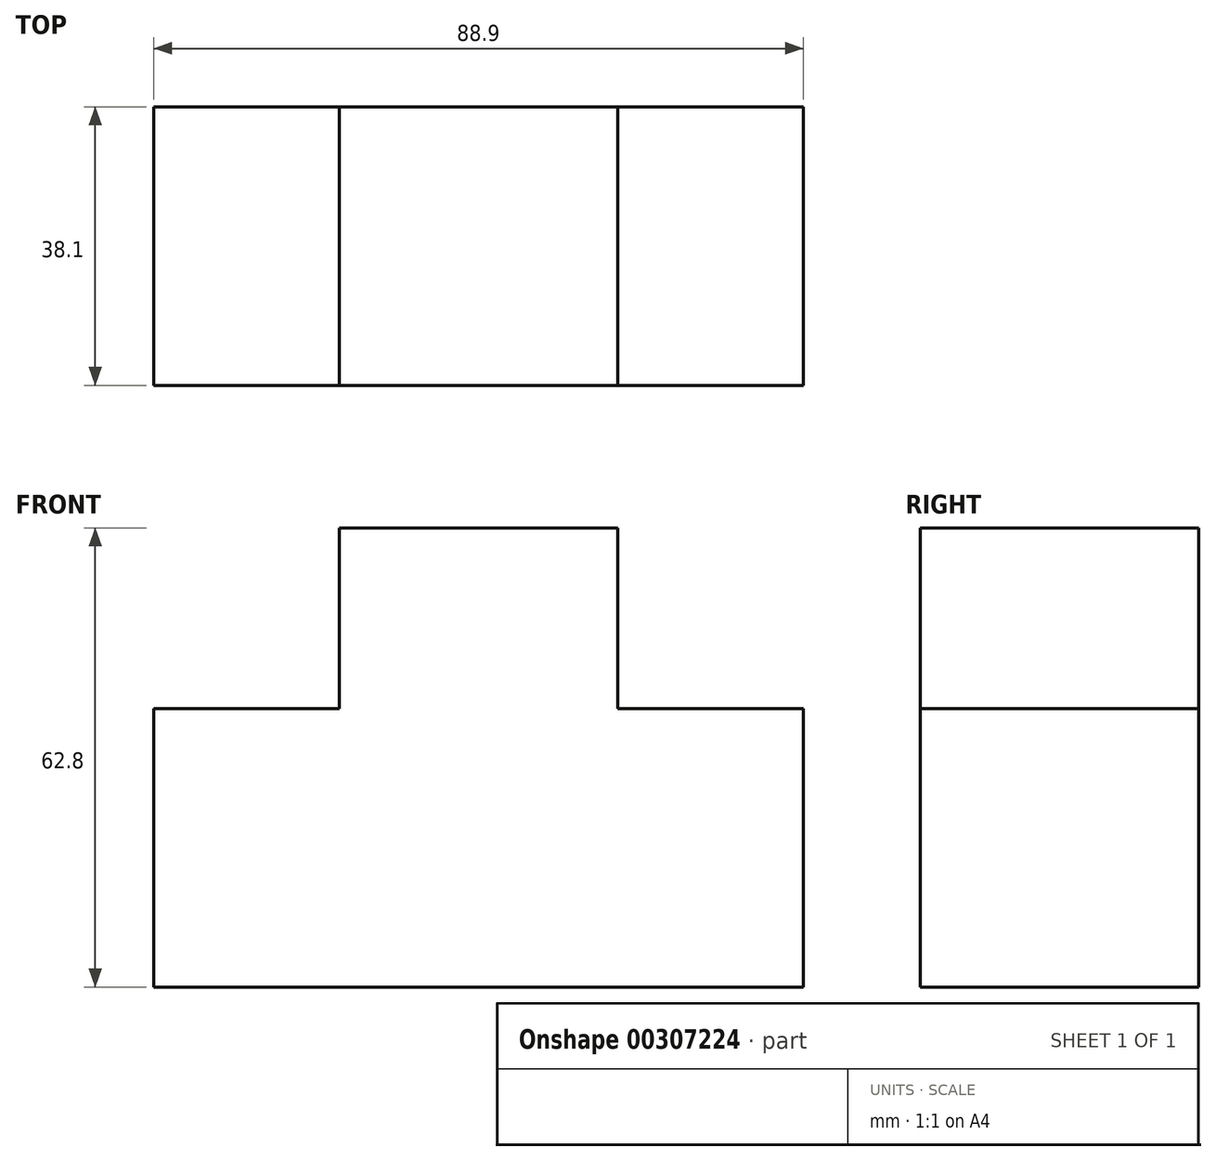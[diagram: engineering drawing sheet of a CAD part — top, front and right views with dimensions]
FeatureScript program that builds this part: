
annotation { "Feature Type Name" : "Feature", "Feature Type Description" : "" }
export const myFeature = defineFeature(function(context is Context, id is Id, definition is map)
    precondition{}
    {
        {
            var Q0;
            Q0=qCreatedBy(makeId("Front.planeOp"),FACE);
            var sketch = newSketch(context, id + "F0", { "sketchPlane" : qUnion([Q0])});
            skLineSegment(sketch, "E0", {"start": v(-42.03, -48.8) * mm, "end": v(46.87, -48.8) * mm});
            skLineSegment(sketch, "E1", {"start": v(46.87, -48.8) * mm, "end": v(46.87, -10.7) * mm});
            skLineSegment(sketch, "E2", {"start": v(46.87, -10.7) * mm, "end": v(21.47, -10.7) * mm});
            skLineSegment(sketch, "E3", {"start": v(21.47, -10.7) * mm, "end": v(21.47, 14) * mm});
            skLineSegment(sketch, "E4", {"start": v(21.47, 14) * mm, "end": v(-16.63, 14) * mm});
            skLineSegment(sketch, "E5", {"start": v(-16.63, 14) * mm, "end": v(-16.63, -10.7) * mm});
            skLineSegment(sketch, "E6", {"start": v(-16.63, -10.7) * mm, "end": v(-42.03, -10.7) * mm});
            skLineSegment(sketch, "E7", {"start": v(-42.03, -10.7) * mm, "end": v(-42.03, -48.8) * mm});
            skSolve(sketch);
        }
        {
            var Q0;
            Q0=makeQuery(id+"F0.imprint","IMPRINT",FACE,{"disambiguationData":[TD([[makeQuery(id+"F0.imprint","IMPRINT",EDGE,{"derivedFrom":sQuery(id+"F0.wireOp",EDGE,"E0")}),1.0]])]});
            extrude(context, id + "F1", {"entities" : qUnion([Q0]), "depth" : 38.1 * mm});
        }
    });
